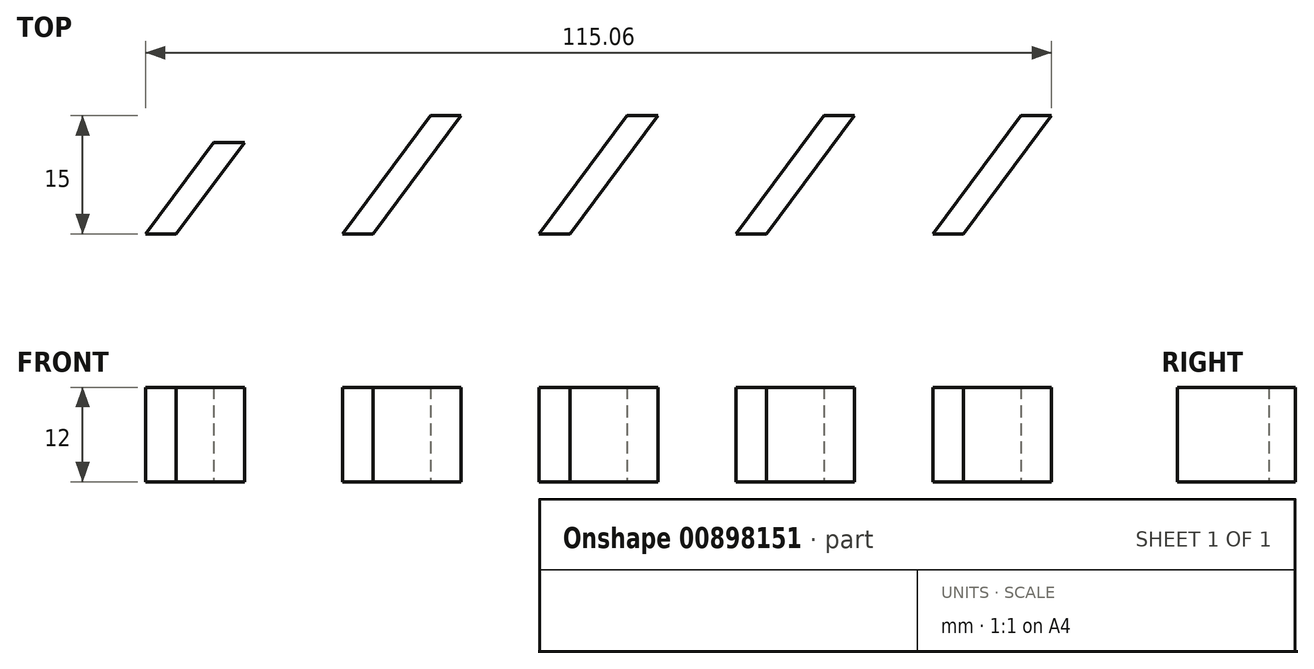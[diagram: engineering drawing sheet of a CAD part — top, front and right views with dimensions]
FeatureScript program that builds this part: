
annotation { "Feature Type Name" : "Feature", "Feature Type Description" : "" }
export const myFeature = defineFeature(function(context is Context, id is Id, definition is map)
    precondition{}
    {
        {
            var Q0;
            Q0=qCreatedBy(makeId("Top.planeOp"),FACE);
            var sketch = newSketch(context, id + "F0", { "sketchPlane" : qUnion([Q0])});
            skLineSegment(sketch, "E0", {"start": v(-61.3, -12) * mm, "end": v(-52.64, -0.38) * mm});
            skLineSegment(sketch, "E1", {"start": v(-52.64, -0.38) * mm, "end": v(-48.76, -0.38) * mm});
            skLineSegment(sketch, "E2", {"start": v(-48.76, -0.38) * mm, "end": v(-57.42, -12) * mm});
            skLineSegment(sketch, "E3.1.0.0", {"start": v(-21.24, 3) * mm, "end": v(-32.42, -12) * mm});
            skLineSegment(sketch, "E3.1.0.1", {"start": v(-25.13, 3) * mm, "end": v(-21.24, 3) * mm});
            skLineSegment(sketch, "E3.1.0.2", {"start": v(-36.3, -12) * mm, "end": v(-25.13, 3) * mm});
            skLineSegment(sketch, "E3.2.0.0", {"start": v(3.76, 3) * mm, "end": v(-7.42, -12) * mm});
            skLineSegment(sketch, "E3.2.0.1", {"start": v(-0.13, 3) * mm, "end": v(3.76, 3) * mm});
            skLineSegment(sketch, "E3.2.0.2", {"start": v(-11.3, -12) * mm, "end": v(-0.13, 3) * mm});
            skLineSegment(sketch, "E3.3.0.0", {"start": v(28.76, 3) * mm, "end": v(17.58, -12) * mm});
            skLineSegment(sketch, "E3.3.0.1", {"start": v(24.87, 3) * mm, "end": v(28.76, 3) * mm});
            skLineSegment(sketch, "E3.3.0.2", {"start": v(13.7, -12) * mm, "end": v(24.87, 3) * mm});
            skLineSegment(sketch, "E3.4.0.0", {"start": v(53.76, 3) * mm, "end": v(42.58, -12) * mm});
            skLineSegment(sketch, "E3.4.0.1", {"start": v(49.87, 3) * mm, "end": v(53.76, 3) * mm});
            skLineSegment(sketch, "E3.4.0.2", {"start": v(38.7, -12) * mm, "end": v(49.87, 3) * mm});
            skLineSegment(sketch, "E4", {"start": v(-61.3, -12) * mm, "end": v(-57.42, -12) * mm});
            skLineSegment(sketch, "E5", {"start": v(-36.3, -12) * mm, "end": v(-32.42, -12) * mm});
            skLineSegment(sketch, "E6", {"start": v(-11.3, -12) * mm, "end": v(-7.42, -12) * mm});
            skLineSegment(sketch, "E7", {"start": v(13.7, -12) * mm, "end": v(17.58, -12) * mm});
            skLineSegment(sketch, "E8", {"start": v(38.7, -12) * mm, "end": v(42.58, -12) * mm});
            skSolve(sketch);
        }
        {
            var Q0;
            Q0=makeQuery(id+"F0.imprint","IMPRINT",FACE,{"disambiguationData":[TD([[makeQuery(id+"F0.imprint","IMPRINT",EDGE,{"derivedFrom":sQuery(id+"F0.wireOp",EDGE,"E3.1.0.0")}),-1.0]])]});
            var Q1;
            Q1=makeQuery(id+"F0.imprint","IMPRINT",FACE,{"disambiguationData":[TD([[makeQuery(id+"F0.imprint","IMPRINT",EDGE,{"derivedFrom":sQuery(id+"F0.wireOp",EDGE,"E3.3.0.0")}),-1.0]])]});
            var Q2;
            Q2=makeQuery(id+"F0.imprint","IMPRINT",FACE,{"disambiguationData":[TD([[makeQuery(id+"F0.imprint","IMPRINT",EDGE,{"derivedFrom":sQuery(id+"F0.wireOp",EDGE,"E3.4.0.0")}),-1.0]])]});
            var Q3;
            Q3=makeQuery(id+"F0.imprint","IMPRINT",FACE,{"disambiguationData":[TD([[makeQuery(id+"F0.imprint","IMPRINT",EDGE,{"derivedFrom":sQuery(id+"F0.wireOp",EDGE,"E3.2.0.0")}),-1.0]])]});
            var Q4;
            Q4=makeQuery(id+"F0.imprint","IMPRINT",FACE,{"disambiguationData":[TD([[makeQuery(id+"F0.imprint","IMPRINT",EDGE,{"derivedFrom":sQuery(id+"F0.wireOp",EDGE,"E0")}),-1.0]])]});
            extrude(context, id + "F1", {"entities" : qUnion([Q0, Q1, Q2, Q3, Q4]), "depth" : 6 * mm, "offsetDistance" : 25 * mm, "hasSecondDirection" : true, "secondDirectionOppositeDirection" : true, "secondDirectionDepth" : 6 * mm});
        }
    });
